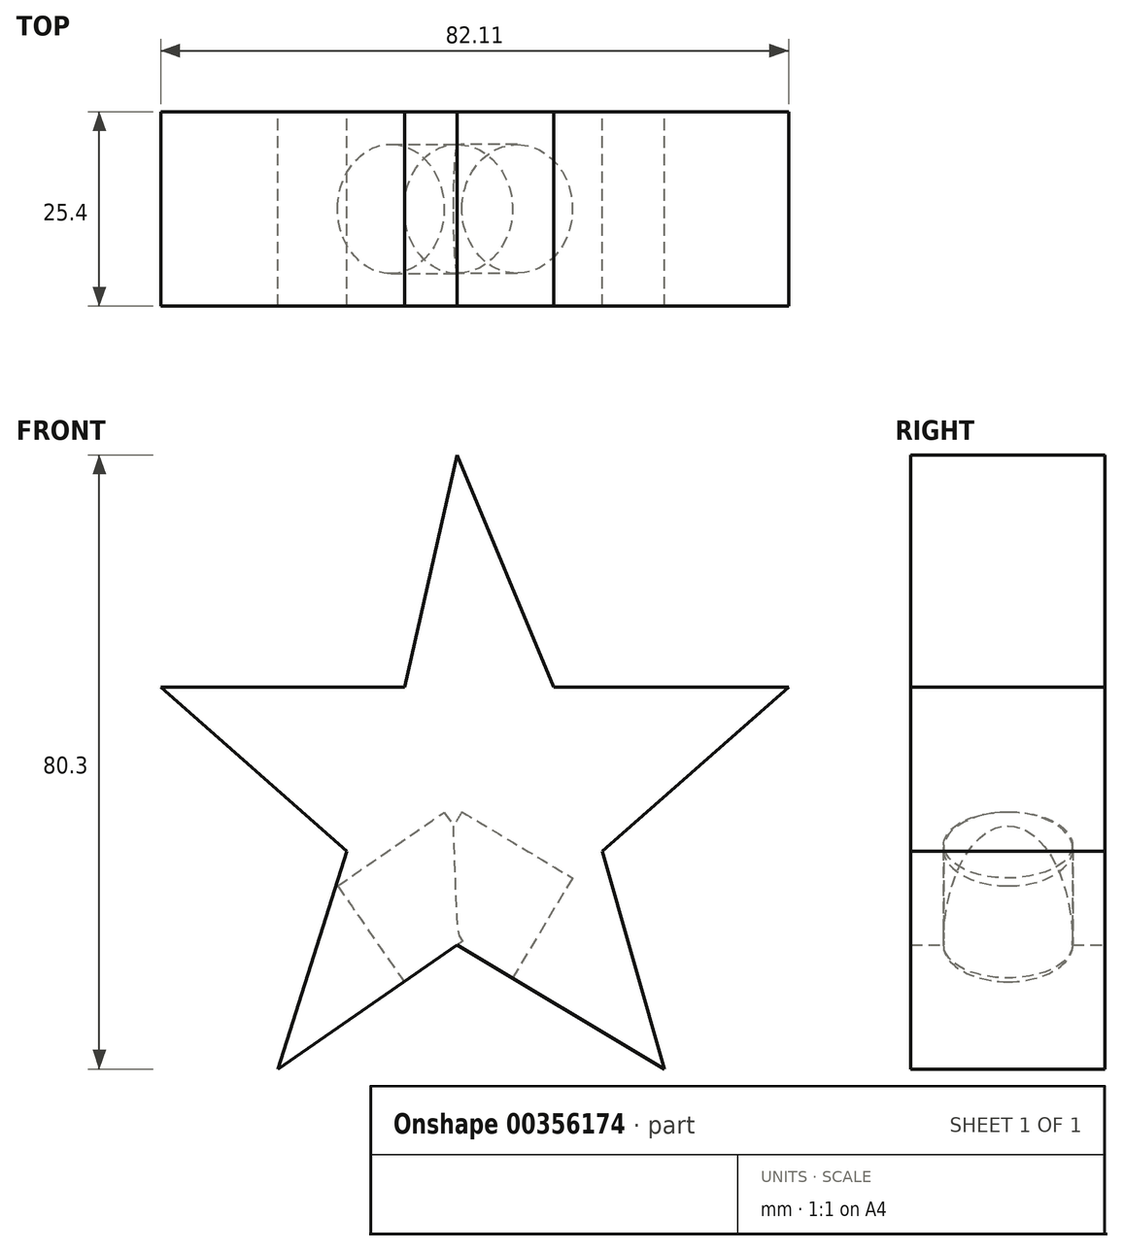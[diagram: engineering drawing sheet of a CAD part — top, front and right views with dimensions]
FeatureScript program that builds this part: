
annotation { "Feature Type Name" : "Feature", "Feature Type Description" : "" }
export const myFeature = defineFeature(function(context is Context, id is Id, definition is map)
    precondition{}
    {
        {
            var Q0;
            Q0=qCreatedBy(makeId("Front.planeOp"),FACE);
            var sketch = newSketch(context, id + "F0", { "sketchPlane" : qUnion([Q0])});
            skPoint(sketch, "E0.end.orphan", {"position": v(-6.89, 21.48) * mm});
            skPoint(sketch, "E1.end.orphan", {"position": v(0, 35.08) * mm});
            skPoint(sketch, "E2.end.orphan", {"position": v(6.7, 20.4) * mm});
            skPoint(sketch, "E3.end.orphan", {"position": v(6.7, 9.46) * mm});
            skPoint(sketch, "E4.start.orphan", {"position": v(-6.89, 9.46) * mm});
            skPoint(sketch, "E5.start.orphan", {"position": v(0, 4.14) * mm});
            skPoint(sketch, "E6.endSnap0", {"position": v(-19.1, 12.04) * mm});
            skPoint(sketch, "E7.start.orphan", {"position": v(-0.1, 9.46) * mm});
            skPoint(sketch, "E8.start.orphan", {"position": v(-19.1, -16) * mm});
            skPoint(sketch, "E9.start.orphan", {"position": v(12.52, -16) * mm});
            skPoint(sketch, "E10.start.orphan", {"position": v(6.7, 21.48) * mm});
            skPoint(sketch, "E11.start.orphan", {"position": v(0, 41.74) * mm});
            skPoint(sketch, "E12.start.orphan", {"position": v(-31.3, 14.61) * mm});
            skPoint(sketch, "E13.end.orphan", {"position": v(21.57, -16) * mm});
            skPoint(sketch, "E14.start.orphan", {"position": v(31.3, 14.61) * mm});
            skLineSegment(sketch, "E15", {"start": v(-6.89, 21.48) * mm, "end": v(0, 51.8) * mm});
            skLineSegment(sketch, "E16", {"start": v(0, 51.8) * mm, "end": v(12.64, 21.48) * mm});
            skLineSegment(sketch, "E17", {"start": v(12.64, 21.48) * mm, "end": v(43.32, 21.48) * mm});
            skLineSegment(sketch, "E18", {"start": v(43.32, 21.48) * mm, "end": v(18.95, 0) * mm});
            skLineSegment(sketch, "E19", {"start": v(18.95, 0) * mm, "end": v(27.07, -28.5) * mm});
            skLineSegment(sketch, "E20", {"start": v(27.07, -28.5) * mm, "end": v(0, -12.25) * mm});
            skLineSegment(sketch, "E21", {"start": v(0, -12.25) * mm, "end": v(-23.45, -28.5) * mm});
            skLineSegment(sketch, "E22", {"start": v(-23.45, -28.5) * mm, "end": v(-14.43, 0) * mm});
            skLineSegment(sketch, "E23", {"start": v(-14.43, 0) * mm, "end": v(-38.8, 21.48) * mm});
            skLineSegment(sketch, "E24", {"start": v(-38.8, 21.48) * mm, "end": v(-6.89, 21.48) * mm});
            skSolve(sketch);
        }
        {
            var Q0;
            Q0 = qSketchRegion(id + "F0", true);
            extrude(context, id + "F1", {"entities" : qUnion([Q0]), "depth" : 25.4 * mm});
        }
        {
            var Q0;
            Q0=makeQuery(id+"F1.opExtrude","SWEPT_FACE",FACE,{"disambiguationData":[OSD([sQuery(id+"F0.wireOp",EDGE,"E20")])]});
            var sketch = newSketch(context, id + "F2", { "sketchPlane" : qUnion([Q0])});
            skCircle(sketch, "E25", {"center": v(6.3, 12.7) * mm, "radius": 8.42 * mm});
            skSolve(sketch);
        }
        {
            var Q0;
            Q0 = qSketchRegion(id + "F2", true);
            extrude(context, id + "F3", {"entities" : qUnion([Q0]), "operationType" : NewBodyOperationType.REMOVE, "oppositeDirection" : true, "depth" : 15.24 * mm});
        }
        {
            var Q0;
            Q0=makeQuery(id+"F1.opExtrude","SWEPT_FACE",FACE,{"disambiguationData":[OSD([sQuery(id+"F0.wireOp",EDGE,"E21")])]});
            var sketch = newSketch(context, id + "F4", { "sketchPlane" : qUnion([Q0])});
            skCircle(sketch, "E26", {"center": v(-6.97, 12.7) * mm, "radius": 8.46 * mm});
            skSolve(sketch);
        }
        {
            var Q0;
            Q0 = qSketchRegion(id + "F4", true);
            extrude(context, id + "F5", {"entities" : qUnion([Q0]), "operationType" : NewBodyOperationType.REMOVE, "oppositeDirection" : true, "depth" : 15.24 * mm});
        }
    });
